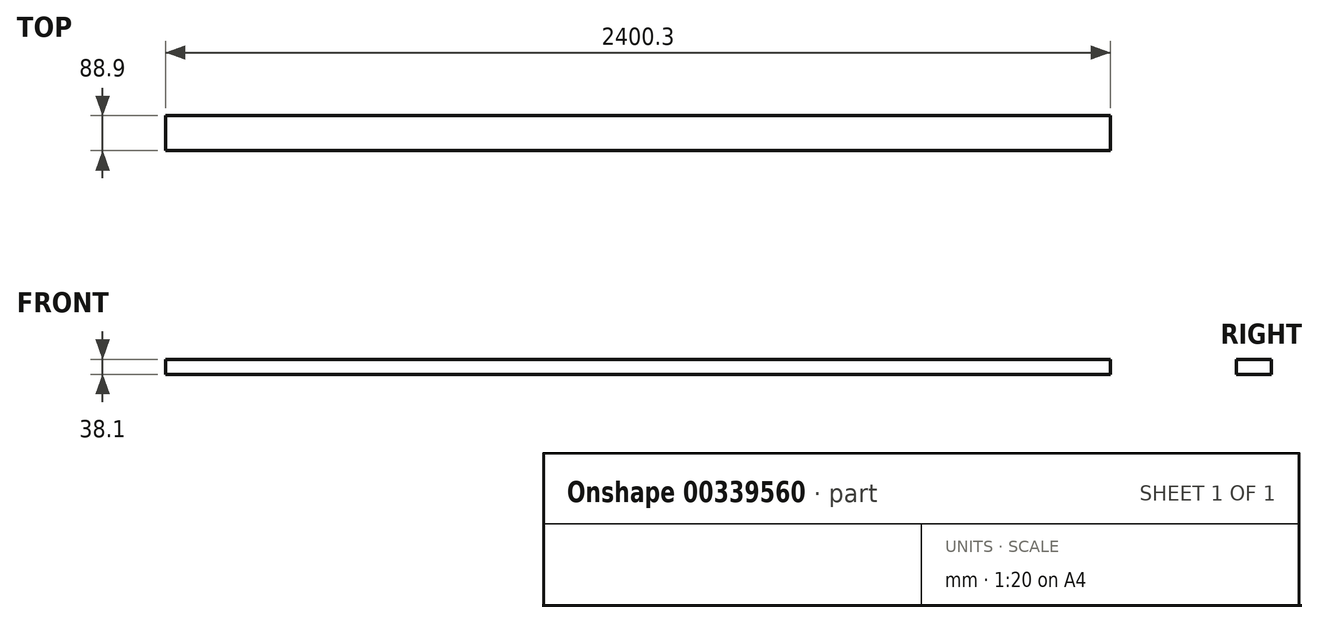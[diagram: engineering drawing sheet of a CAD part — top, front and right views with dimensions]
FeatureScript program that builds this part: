
annotation { "Feature Type Name" : "Feature", "Feature Type Description" : "" }
export const myFeature = defineFeature(function(context is Context, id is Id, definition is map)
    precondition{}
    {
        {
            var Q0;
            Q0=qCreatedBy(makeId("Right.planeOp"),FACE);
            var sketch = newSketch(context, id + "F0", { "sketchPlane" : qUnion([Q0])});
            skLineSegment(sketch, "E0.bottom", {"start": v(-54.1, 21.98) * mm, "end": v(34.8, 21.98) * mm});
            skLineSegment(sketch, "E0.top", {"start": v(-54.1, -16.12) * mm, "end": v(34.8, -16.12) * mm});
            skLineSegment(sketch, "E0.left", {"start": v(-54.1, 21.98) * mm, "end": v(-54.1, -16.12) * mm});
            skLineSegment(sketch, "E0.right", {"start": v(34.8, 21.98) * mm, "end": v(34.8, -16.12) * mm});
            skSolve(sketch);
        }
        {
            var Q0;
            Q0 = qSketchRegion(id + "F0", true);
            extrude(context, id + "F1", {"entities" : qUnion([Q0]), "depth" : 2400.3 * mm});
        }
    });
